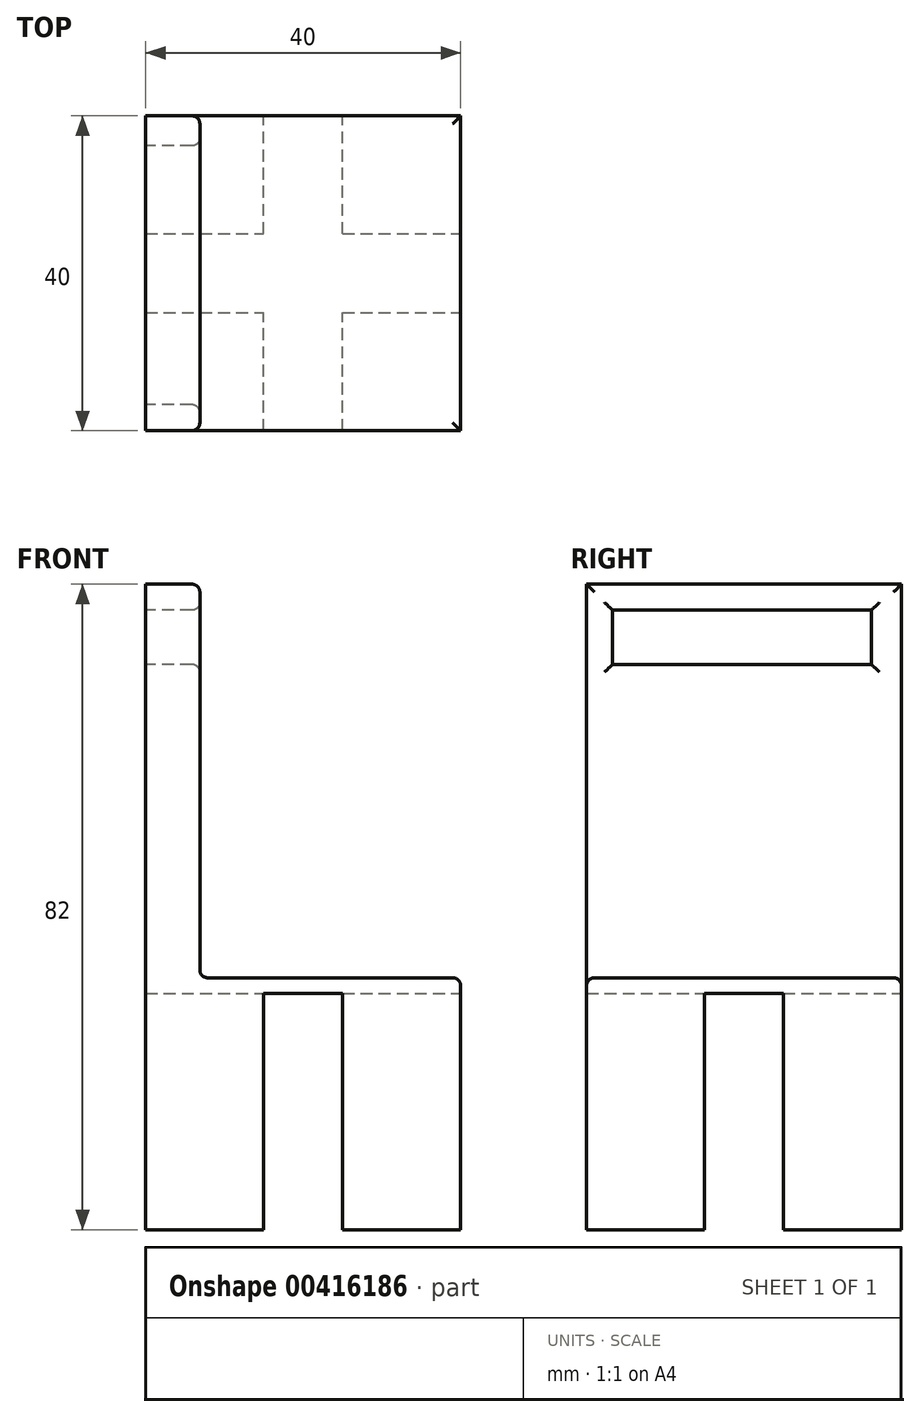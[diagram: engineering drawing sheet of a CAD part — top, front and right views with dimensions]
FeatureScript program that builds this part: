
annotation { "Feature Type Name" : "Feature", "Feature Type Description" : "" }
export const myFeature = defineFeature(function(context is Context, id is Id, definition is map)
    precondition{}
    {
        {
            var Q0;
            Q0=qCreatedBy(makeId("Top.planeOp"),FACE);
            var sketch = newSketch(context, id + "F0", { "sketchPlane" : qUnion([Q0])});
            skLineSegment(sketch, "E0.bottom", {"start": v(10, 10) * mm, "end": v(25, 10) * mm});
            skLineSegment(sketch, "E0.top", {"start": v(10, 25) * mm, "end": v(25, 25) * mm});
            skLineSegment(sketch, "E0.left", {"start": v(10, 10) * mm, "end": v(10, 25) * mm});
            skLineSegment(sketch, "E0.right", {"start": v(25, 10) * mm, "end": v(25, 25) * mm});
            skLineSegment(sketch, "E1.0.1.0", {"start": v(25, 35) * mm, "end": v(25, 50) * mm});
            skLineSegment(sketch, "E1.0.1.1", {"start": v(10, 35) * mm, "end": v(25, 35) * mm});
            skLineSegment(sketch, "E1.0.1.2", {"start": v(10, 35) * mm, "end": v(10, 50) * mm});
            skLineSegment(sketch, "E1.0.1.3", {"start": v(10, 50) * mm, "end": v(25, 50) * mm});
            skLineSegment(sketch, "E1.1.0.0", {"start": v(50, 10) * mm, "end": v(50, 25) * mm});
            skLineSegment(sketch, "E1.1.0.1", {"start": v(35, 10) * mm, "end": v(50, 10) * mm});
            skLineSegment(sketch, "E1.1.0.2", {"start": v(35, 10) * mm, "end": v(35, 25) * mm});
            skLineSegment(sketch, "E1.1.0.3", {"start": v(35, 25) * mm, "end": v(50, 25) * mm});
            skLineSegment(sketch, "E1.1.1.0", {"start": v(50, 35) * mm, "end": v(50, 50) * mm});
            skLineSegment(sketch, "E1.1.1.1", {"start": v(35, 35) * mm, "end": v(50, 35) * mm});
            skLineSegment(sketch, "E1.1.1.2", {"start": v(35, 35) * mm, "end": v(35, 50) * mm});
            skLineSegment(sketch, "E1.1.1.3", {"start": v(35, 50) * mm, "end": v(50, 50) * mm});
            skLineSegment(sketch, "E1.direction1", {"start": v(25, 10) * mm, "end": v(50, 10) * mm, "construction": true});
            skLineSegment(sketch, "E1.direction2", {"start": v(25, 10) * mm, "end": v(25, 35) * mm, "construction": true});
            skSolve(sketch);
        }
        {
            var Q0;
            Q0=makeQuery(id+"F0.imprint","IMPRINT",FACE,{"disambiguationData":[TD([[makeQuery(id+"F0.imprint","IMPRINT",EDGE,{"derivedFrom":sQuery(id+"F0.wireOp",EDGE,"E1.1.0.0")}),1.0]])]});
            var Q1;
            Q1=makeQuery(id+"F0.imprint","IMPRINT",FACE,{"disambiguationData":[TD([[makeQuery(id+"F0.imprint","IMPRINT",EDGE,{"derivedFrom":sQuery(id+"F0.wireOp",EDGE,"E0.bottom")}),1.0]])]});
            var Q2;
            Q2=makeQuery(id+"F0.imprint","IMPRINT",FACE,{"disambiguationData":[TD([[makeQuery(id+"F0.imprint","IMPRINT",EDGE,{"derivedFrom":sQuery(id+"F0.wireOp",EDGE,"E1.0.1.0")}),1.0]])]});
            var Q3;
            Q3=makeQuery(id+"F0.imprint","IMPRINT",FACE,{"disambiguationData":[TD([[makeQuery(id+"F0.imprint","IMPRINT",EDGE,{"derivedFrom":sQuery(id+"F0.wireOp",EDGE,"E1.1.1.0")}),1.0]])]});
            extrude(context, id + "F1", {"entities" : qUnion([Q0, Q1, Q2, Q3]), "depth" : 30 * mm});
        }
        {
            var Q0;
            Q0=makeQuery(id+"F1.opExtrude","CAP_FACE",FACE,{"disambiguationData":[OSD([sQuery(id+"F0.wireOp",EDGE,"E1.1.0.0"),sQuery(id+"F0.wireOp",EDGE,"E1.1.0.1"),sQuery(id+"F0.wireOp",EDGE,"E1.1.0.2"),sQuery(id+"F0.wireOp",EDGE,"E1.1.0.3")])],"isStart":false});
            var sketch = newSketch(context, id + "F2", { "sketchPlane" : qUnion([Q0])});
            skLineSegment(sketch, "E2.bottom", {"start": v(50, 10) * mm, "end": v(10, 10) * mm});
            skLineSegment(sketch, "E2.top", {"start": v(50, 50) * mm, "end": v(10, 50) * mm});
            skLineSegment(sketch, "E2.left", {"start": v(50, 10) * mm, "end": v(50, 50) * mm});
            skLineSegment(sketch, "E2.right", {"start": v(10, 10) * mm, "end": v(10, 50) * mm});
            skSolve(sketch);
        }
        {
            var Q0;
            {var subQ3=makeQuery(id+"F1.opExtrude","CAP_EDGE",EDGE,{"disambiguationData":[OSD([sQuery(id+"F0.wireOp",EDGE,"E1.1.0.2")])],"isStart":false});Q0=makeQuery(id+"F2.imprint","IMPRINT",FACE,{"disambiguationData":[TD([[makeQuery(id+"F2.imprint","IMPRINT",EDGE,{"derivedFrom":subQ3}),-1.0]])]});}
            var Q1;
            {var subQ3=sQuery(id+"F2.wireOp",EDGE,"E2.top");Q1=makeQuery(id+"F2.imprint","IMPRINT",FACE,{"disambiguationData":[TD([[makeQuery(id+"F2.imprint","IMPRINT",EDGE,{"derivedFrom":subQ3}),1.0]])]});}
            extrude(context, id + "F3", {"entities" : qUnion([Q0, Q1]), "operationType" : NewBodyOperationType.ADD, "depth" : 2 * mm});
        }
        {
            var Q0;
            Q0=makeQuery(id+"F3.opExtrude","CAP_FACE",FACE,{"disambiguationData":[OSD([sQuery(id+"F2.wireOp",EDGE,"E2.bottom"),sQuery(id+"F2.wireOp",EDGE,"E2.top"),sQuery(id+"F2.wireOp",EDGE,"E2.left"),sQuery(id+"F2.wireOp",EDGE,"E2.right")])],"isStart":false});
            var sketch = newSketch(context, id + "F4", { "sketchPlane" : qUnion([Q0])});
            skLineSegment(sketch, "E3.bottom", {"start": v(10, 10) * mm, "end": v(16.88, 10) * mm});
            skLineSegment(sketch, "E3.top", {"start": v(10, 50) * mm, "end": v(16.88, 50) * mm});
            skLineSegment(sketch, "E3.left", {"start": v(10, 10) * mm, "end": v(10, 50) * mm});
            skLineSegment(sketch, "E3.right", {"start": v(16.88, 10) * mm, "end": v(16.88, 50) * mm});
            skSolve(sketch);
        }
        {
            var Q0;
            Q0=makeQuery(id+"F4.imprint","IMPRINT",FACE,{"disambiguationData":[TD([[makeQuery(id+"F4.imprint","IMPRINT",EDGE,{"derivedFrom":sQuery(id+"F4.wireOp",EDGE,"E3.bottom")}),1.0]])]});
            extrude(context, id + "F5", {"entities" : qUnion([Q0]), "operationType" : NewBodyOperationType.ADD, "depth" : 50 * mm});
        }
        {
            var Q0;
            Q0=makeQuery(id+"F5.boolean.opBoolean","MERGE",FACE,{"derivedFrom":[makeQuery(id+"F3.boolean.opBoolean","MERGE",FACE,{"derivedFrom":[makeQuery(id+"F1.opExtrude","SWEPT_FACE",FACE,{"disambiguationData":[OSD([sQuery(id+"F0.wireOp",EDGE,"E0.left")])]}),makeQuery(id+"F1.opExtrude","SWEPT_FACE",FACE,{"disambiguationData":[OSD([sQuery(id+"F0.wireOp",EDGE,"E1.0.1.2")])]}),makeQuery(id+"F3.opExtrude","SWEPT_FACE",FACE,{"disambiguationData":[OSD([sQuery(id+"F2.wireOp",EDGE,"E2.right")])]})]}),makeQuery(id+"F5.opExtrude","SWEPT_FACE",FACE,{"disambiguationData":[OSD([sQuery(id+"F4.wireOp",EDGE,"E3.left")])]})]});
            var sketch = newSketch(context, id + "F6", { "sketchPlane" : qUnion([Q0])});
            skLineSegment(sketch, "E4.bottom", {"start": v(-46.2, 78.7) * mm, "end": v(-13.3, 78.7) * mm});
            skLineSegment(sketch, "E4.top", {"start": v(-46.2, 71.81) * mm, "end": v(-13.3, 71.81) * mm});
            skLineSegment(sketch, "E4.left", {"start": v(-46.2, 78.7) * mm, "end": v(-46.2, 71.81) * mm});
            skLineSegment(sketch, "E4.right", {"start": v(-13.3, 78.7) * mm, "end": v(-13.3, 71.81) * mm});
            skSolve(sketch);
        }
        {
            var Q0;
            Q0=makeQuery(id+"F6.imprint","IMPRINT",FACE,{"disambiguationData":[TD([[makeQuery(id+"F6.imprint","IMPRINT",EDGE,{"derivedFrom":sQuery(id+"F6.wireOp",EDGE,"E4.bottom")}),-1.0]])]});
            extrude(context, id + "F7", {"entities" : qUnion([Q0]), "operationType" : NewBodyOperationType.REMOVE, "oppositeDirection" : true, "depth" : 30 * mm});
        }
        {
            var Q0;
            Q0=makeQuery(id+"F3.opExtrude","CAP_FACE",FACE,{"disambiguationData":[OSD([sQuery(id+"F2.wireOp",EDGE,"E2.bottom"),sQuery(id+"F2.wireOp",EDGE,"E2.top"),sQuery(id+"F2.wireOp",EDGE,"E2.left"),sQuery(id+"F2.wireOp",EDGE,"E2.right")])],"isStart":false});
            var Q1;
            Q1=makeQuery(id+"F5.opExtrude","SWEPT_FACE",FACE,{"disambiguationData":[OSD([sQuery(id+"F4.wireOp",EDGE,"E3.right")])]});
            fillet(context, id + "F8", {"entities" : qUnion([Q0, Q1]), "radius" : 1 * mm, "tangentPropagation" : true, "allowEdgeOverflow" : false});
        }
    });
